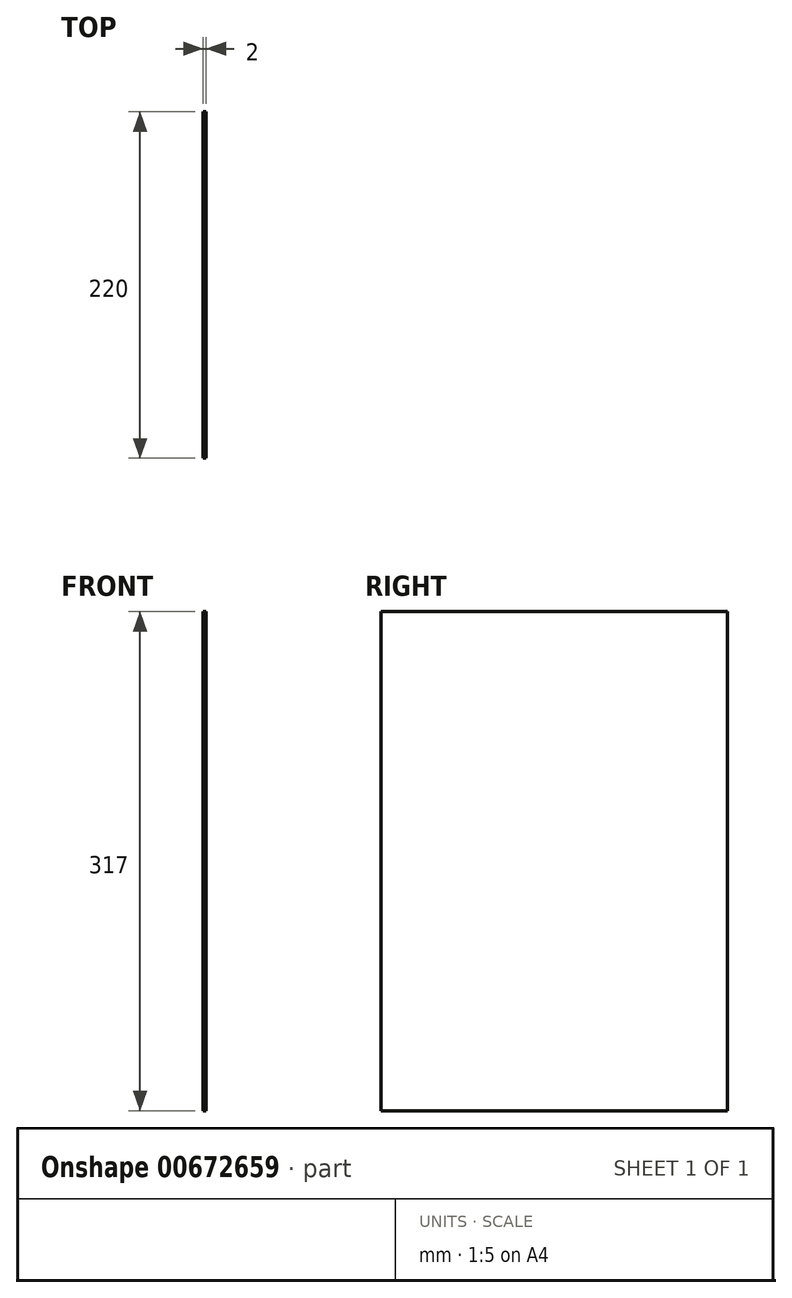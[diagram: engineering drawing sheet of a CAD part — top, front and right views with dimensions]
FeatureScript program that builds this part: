
annotation { "Feature Type Name" : "Feature", "Feature Type Description" : "" }
export const myFeature = defineFeature(function(context is Context, id is Id, definition is map)
    precondition{}
    {
        {
            var Q0;
            Q0=qCreatedBy(makeId("Right.planeOp"),FACE);
            var sketch = newSketch(context, id + "F0", { "sketchPlane" : qUnion([Q0])});
            skLineSegment(sketch, "E0.bottom", {"start": v(-106, 227.72) * mm, "end": v(114, 227.72) * mm});
            skLineSegment(sketch, "E0.top", {"start": v(-106, -89.28) * mm, "end": v(114, -89.28) * mm});
            skLineSegment(sketch, "E0.left", {"start": v(-106, 227.72) * mm, "end": v(-106, -89.28) * mm});
            skLineSegment(sketch, "E0.right", {"start": v(114, 227.72) * mm, "end": v(114, -89.28) * mm});
            skSolve(sketch);
        }
        {
            var Q0;
            Q0 = qSketchRegion(id + "F0", true);
            extrude(context, id + "F1", {"entities" : qUnion([Q0]), "depth" : 2 * mm, "offsetDistance" : 25 * mm});
        }
    });
